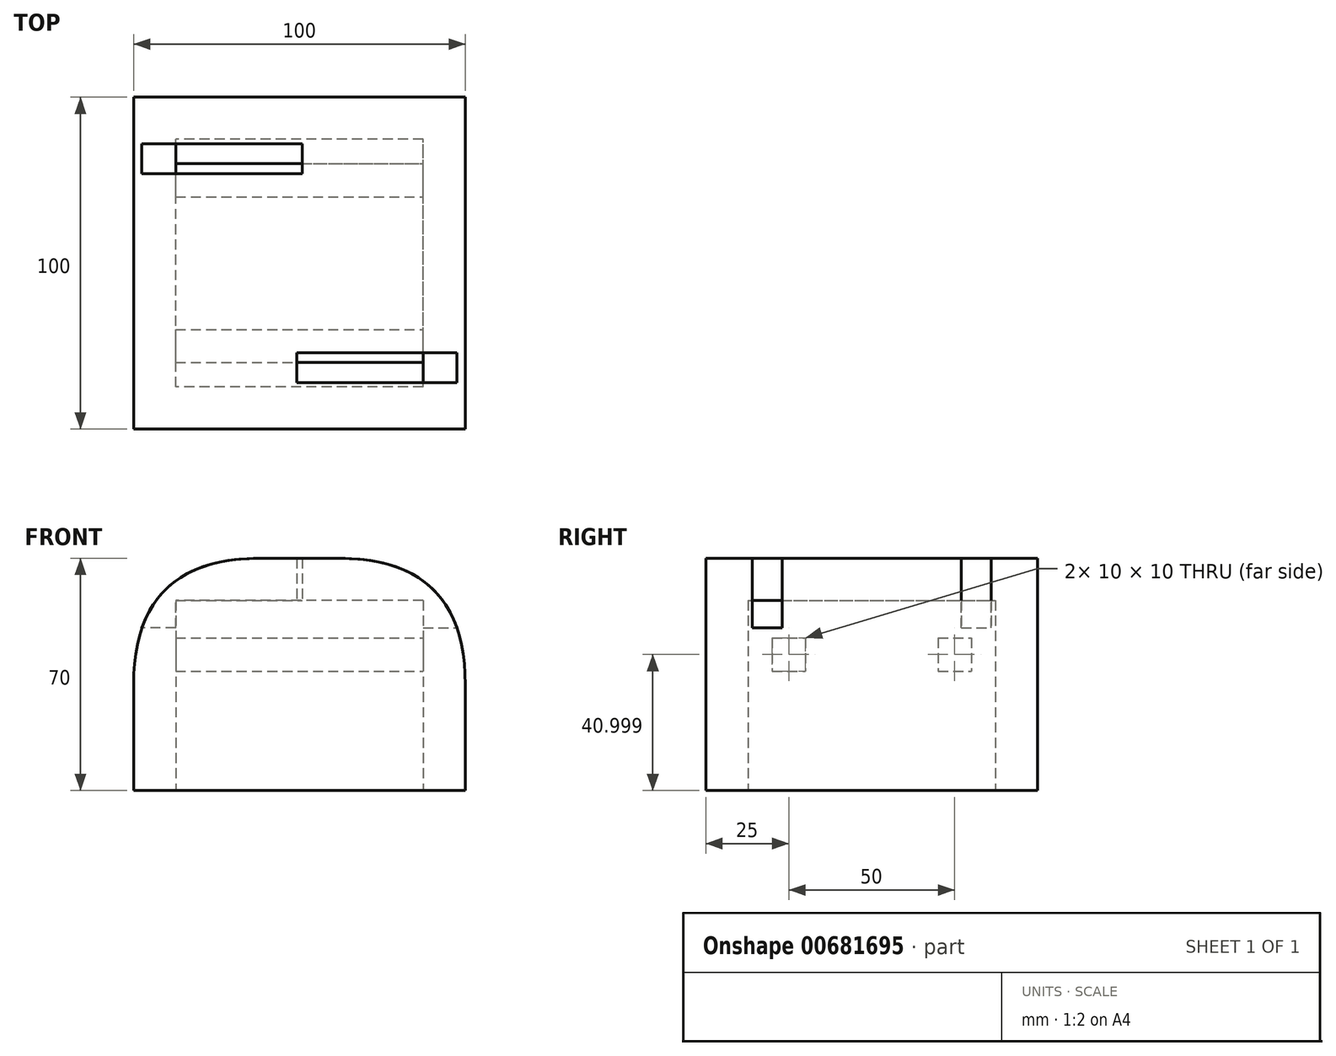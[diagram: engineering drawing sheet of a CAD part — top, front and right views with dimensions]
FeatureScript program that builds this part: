
annotation { "Feature Type Name" : "Feature", "Feature Type Description" : "" }
export const myFeature = defineFeature(function(context is Context, id is Id, definition is map)
    precondition{}
    {
        {
            var Q0;
            Q0=qCreatedBy(makeId("Front.planeOp"),FACE);
            var sketch = newSketch(context, id + "F0", { "sketchPlane" : qUnion([Q0])});
            skLineSegment(sketch, "E0.bottom", {"start": v(34.09, -17.92) * mm, "end": v(-65.91, -17.92) * mm});
            skLineSegment(sketch, "E0.top", {"start": v(34.09, -87.92) * mm, "end": v(-65.91, -87.92) * mm});
            skLineSegment(sketch, "E0.left", {"start": v(34.09, -17.92) * mm, "end": v(34.09, -87.92) * mm});
            skLineSegment(sketch, "E0.right", {"start": v(-65.91, -17.92) * mm, "end": v(-65.91, -87.92) * mm});
            skSolve(sketch);
        }
        {
            var Q0;
            Q0=makeQuery(id+"F0.imprint","IMPRINT",FACE,{"disambiguationData":[TD([[makeQuery(id+"F0.imprint","IMPRINT",EDGE,{"derivedFrom":sQuery(id+"F0.wireOp",EDGE,"E0.bottom")}),1.0]])]});
            extrude(context, id + "F1", {"entities" : qUnion([Q0]), "depth" : 100 * mm, "offsetDistance" : 25.4 * mm});
        }
        {
            var Q0;
            Q0=makeQuery(id+"F1.opExtrude","SWEPT_FACE",FACE,{"disambiguationData":[OSD([sQuery(id+"F0.wireOp",EDGE,"E0.top")])]});
            shell(context, id + "F2", {"entities" : qUnion([Q0]), "thickness" : 12.7 * mm});
        }
        {
            var Q0;
            Q0=makeQuery(id+"F1.opExtrude","SWEPT_EDGE",EDGE,{"disambiguationData":[OSD([sQuery(id+"F0.wireOp",EDGE,"E0.bottom"),sQuery(id+"F0.wireOp",EDGE,"E0.left")])]});
            fillet(context, id + "F3", {"entities" : qUnion([Q0]), "radius" : 38.1 * mm, "tangentPropagation" : true, "rho" : 0.5, "crossSection" : FilletCrossSection.CONIC, "allowEdgeOverflow" : false});
        }
        {
            var Q0;
            Q0=makeQuery(id+"F1.opExtrude","SWEPT_EDGE",EDGE,{"disambiguationData":[OSD([sQuery(id+"F0.wireOp",EDGE,"E0.bottom"),sQuery(id+"F0.wireOp",EDGE,"E0.right")])]});
            fillet(context, id + "F4", {"entities" : qUnion([Q0]), "radius" : 38.1 * mm, "tangentPropagation" : true, "rho" : 0.5, "crossSection" : FilletCrossSection.CONIC, "allowEdgeOverflow" : false});
        }
        {
            var Q0;
            Q0=makeQuery(id+"F1.opExtrude","SWEPT_FACE",FACE,{"disambiguationData":[OSD([sQuery(id+"F0.wireOp",EDGE,"E0.right")])]});
            var sketch = newSketch(context, id + "F5", { "sketchPlane" : qUnion([Q0])});
            skLineSegment(sketch, "E1.bottom", {"start": v(14, -6.92) * mm, "end": v(23, -6.92) * mm});
            skLineSegment(sketch, "E1.top", {"start": v(14, -38.92) * mm, "end": v(23, -38.92) * mm});
            skLineSegment(sketch, "E1.left", {"start": v(14, -6.92) * mm, "end": v(14, -38.92) * mm});
            skLineSegment(sketch, "E1.right", {"start": v(23, -6.92) * mm, "end": v(23, -38.92) * mm});
            skSolve(sketch);
        }
        {
            var Q0;
            Q0=qSketchRegion(id+"F5",true);
            extrude(context, id + "F6", {"entities" : qUnion([Q0]), "operationType" : NewBodyOperationType.REMOVE, "oppositeDirection" : true, "depth" : 50.8 * mm, "offsetDistance" : 25.4 * mm});
        }
        {
            var Q0;
            Q0=makeQuery(id+"F1.opExtrude","SWEPT_FACE",FACE,{"disambiguationData":[OSD([sQuery(id+"F0.wireOp",EDGE,"E0.left")])]});
            var sketch = newSketch(context, id + "F7", { "sketchPlane" : qUnion([Q0])});
            skLineSegment(sketch, "E2.bottom", {"start": v(-86, -8.92) * mm, "end": v(-77, -8.92) * mm});
            skLineSegment(sketch, "E2.top", {"start": v(-86, -38.92) * mm, "end": v(-77, -38.92) * mm});
            skLineSegment(sketch, "E2.left", {"start": v(-86, -8.92) * mm, "end": v(-86, -38.92) * mm});
            skLineSegment(sketch, "E2.right", {"start": v(-77, -8.92) * mm, "end": v(-77, -38.92) * mm});
            skSolve(sketch);
        }
        {
            var Q0;
            Q0=qSketchRegion(id+"F7",true);
            extrude(context, id + "F8", {"entities" : qUnion([Q0]), "operationType" : NewBodyOperationType.REMOVE, "oppositeDirection" : true, "depth" : 50.8 * mm, "offsetDistance" : 25.4 * mm});
        }
        {
            var Q0;
            Q0=makeQuery(id+"F2.opShell","OFFSET_FACE",FACE,{"disambiguationData":[OSD([sQuery(id+"F0.wireOp",EDGE,"E0.left")])]});
            var sketch = newSketch(context, id + "F9", { "sketchPlane" : qUnion([Q0])});
            skLineSegment(sketch, "E3.left", {"start": v(20, -41.92) * mm, "end": v(20, -51.92) * mm});
            skLineSegment(sketch, "E3.right", {"start": v(80, -41.92) * mm, "end": v(80, -51.92) * mm});
            skLineSegment(sketch, "E4", {"start": v(70, -41.92) * mm, "end": v(70, -51.92) * mm});
            skLineSegment(sketch, "E5", {"start": v(30, -41.92) * mm, "end": v(30, -51.92) * mm});
            skLineSegment(sketch, "E6", {"start": v(80, -41.92) * mm, "end": v(70, -41.92) * mm});
            skLineSegment(sketch, "E7", {"start": v(80, -51.92) * mm, "end": v(70, -51.92) * mm});
            skLineSegment(sketch, "E8", {"start": v(30, -41.92) * mm, "end": v(20, -41.92) * mm});
            skLineSegment(sketch, "E9", {"start": v(30, -51.92) * mm, "end": v(20, -51.92) * mm});
            skSolve(sketch);
        }
        {
            var Q0;
            Q0=makeQuery(id+"F1.opExtrude","CAP_FACE",FACE,{"disambiguationData":[OSD([sQuery(id+"F0.wireOp",EDGE,"E0.bottom"),sQuery(id+"F0.wireOp",EDGE,"E0.top"),sQuery(id+"F0.wireOp",EDGE,"E0.left"),sQuery(id+"F0.wireOp",EDGE,"E0.right")])],"isStart":false});
            var sketch = newSketch(context, id + "F10", { "sketchPlane" : qUnion([Q0])});
            skLineSegment(sketch, "E10.bottom", {"start": v(-74.81, -11.72) * mm, "end": v(220.59, -11.72) * mm});
            skLineSegment(sketch, "E10.top", {"start": v(-74.81, -87.92) * mm, "end": v(220.59, -87.92) * mm});
            skLineSegment(sketch, "E10.left", {"start": v(-74.81, -11.72) * mm, "end": v(-74.81, -87.92) * mm});
            skLineSegment(sketch, "E10.right", {"start": v(220.59, -11.72) * mm, "end": v(220.59, -87.92) * mm});
            skSolve(sketch);
        }
        {
            var Q0;
            {var subQ0=sQuery(id+"F10.wireOp",EDGE,"E10.bottom");var subQ1=makeQuery(id+"F1.opExtrude","CAP_EDGE",EDGE,{"disambiguationData":[OSD([sQuery(id+"F0.wireOp",EDGE,"E0.right")])],"isStart":false});var subQ2=makeQuery(id+"F10.imprint","INTERSECT",VERTEX,{"derivedFrom":[subQ1,subQ0]});Q0=makeQuery(id+"F10.imprint","IMPRINT",FACE,{"disambiguationData":[TD([[makeQuery(id+"F10.imprint","IMPRINT",EDGE,{"disambiguationData":[TD([[subQ2,-1.0]])],"derivedFrom":subQ0}),-1.0]])]});}
            extrude(context, id + "F11", {"entities" : qUnion([Q0]), "operationType" : NewBodyOperationType.REMOVE, "oppositeDirection" : true, "depth" : 180.34 * mm, "offsetDistance" : 25.4 * mm});
        }
        {
            var Q0;
            Q0 = qSketchRegion(id + "F9", true);
            extrude(context, id + "F12", {"entities" : qUnion([Q0]), "operationType" : NewBodyOperationType.ADD, "depth" : 83.82 * mm, "offsetDistance" : 25.4 * mm});
        }
    });
